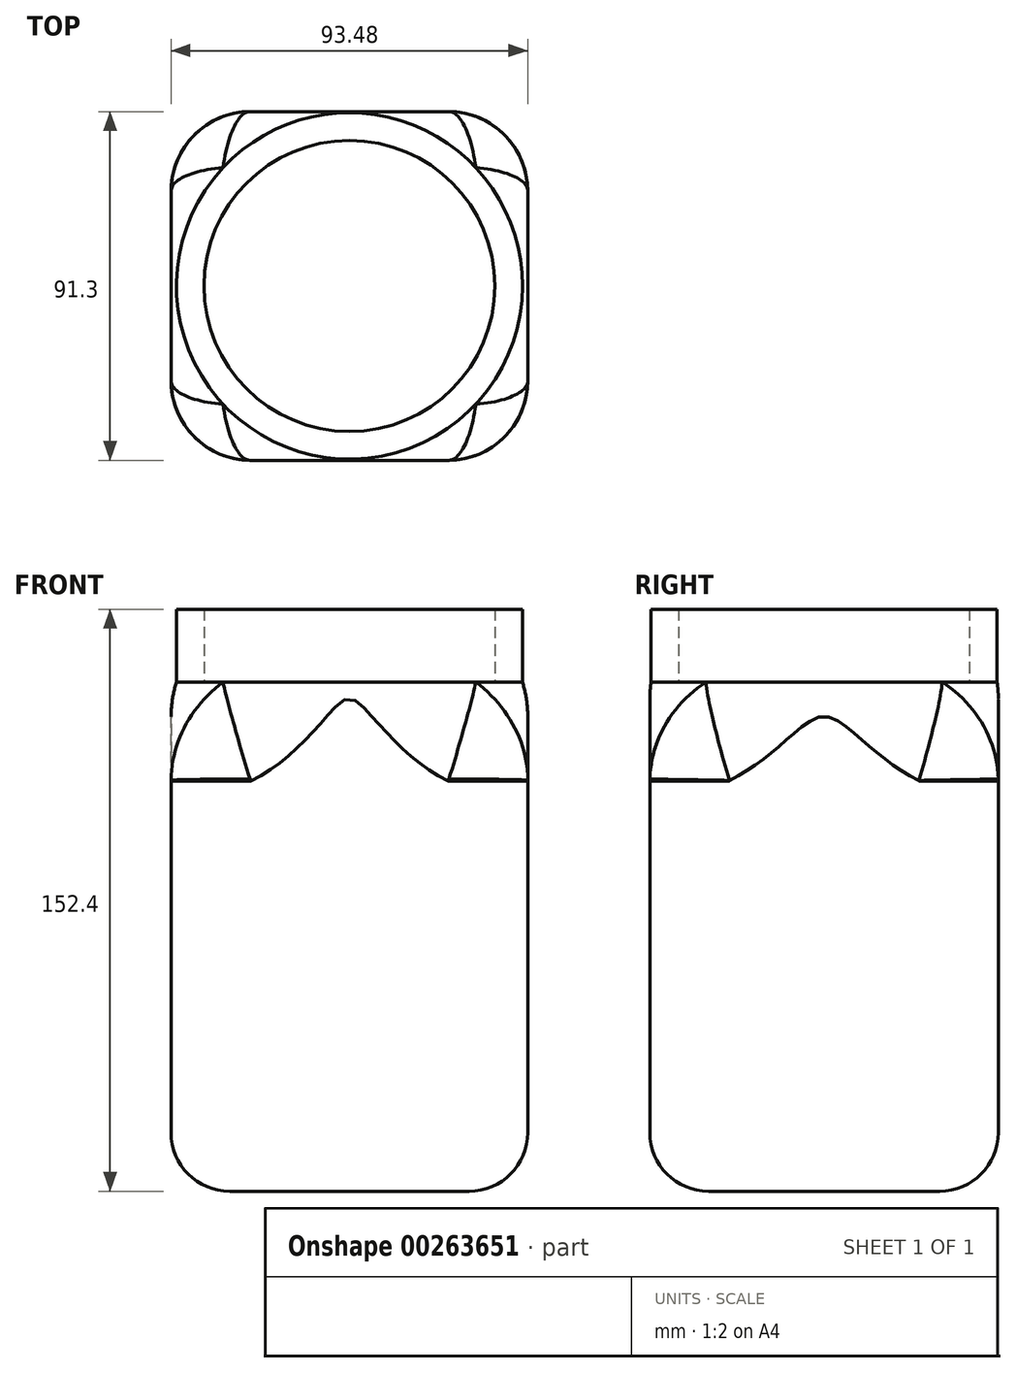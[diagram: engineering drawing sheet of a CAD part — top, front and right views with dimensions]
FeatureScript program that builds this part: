
annotation { "Feature Type Name" : "Feature", "Feature Type Description" : "" }
export const myFeature = defineFeature(function(context is Context, id is Id, definition is map)
    precondition{}
    {
        {
            var Q0;
            Q0=qCreatedBy(makeId("Top.planeOp"),FACE);
            var sketch = newSketch(context, id + "F0", { "sketchPlane" : qUnion([Q0])});
            skCircle(sketch, "E0", {"center": v(0, 0) * mm, "radius": 45.34 * mm});
            skSolve(sketch);
        }
        {
            var Q0;
            Q0 = qSketchRegion(id + "F0", true);
            extrude(context, id + "F1", {"entities" : qUnion([Q0]), "depth" : 19.05 * mm});
        }
        {
            var Q0;
            Q0=qCreatedBy(makeId("Top.planeOp"),FACE);
            var sketch = newSketch(context, id + "F2", { "sketchPlane" : qUnion([Q0])});
            skLineSegment(sketch, "E1.bottom", {"start": v(46.74, -45.65) * mm, "end": v(-46.74, -45.65) * mm});
            skLineSegment(sketch, "E1.top", {"start": v(46.74, 45.65) * mm, "end": v(-46.74, 45.65) * mm});
            skLineSegment(sketch, "E1.left", {"start": v(46.74, -45.65) * mm, "end": v(46.74, 45.65) * mm});
            skLineSegment(sketch, "E1.right", {"start": v(-46.74, -45.65) * mm, "end": v(-46.74, 45.65) * mm});
            skPoint(sketch, "E1.middle", {"position": v(0, 0) * mm});
            skSolve(sketch);
        }
        {
            var Q0;
            Q0=makeQuery(id+"F2.imprint","IMPRINT",FACE,{"disambiguationData":[TD([[makeQuery(id+"F2.imprint","IMPRINT",EDGE,{"derivedFrom":sQuery(id+"F2.wireOp",EDGE,"E1.bottom")}),-1.0]])]});
            extrude(context, id + "F3", {"entities" : qUnion([Q0]), "operationType" : NewBodyOperationType.ADD, "oppositeDirection" : true, "depth" : 133.35 * mm});
        }
        {
            var Q0;
            Q0=makeQuery(id+"F3.opExtrude","SWEPT_EDGE",EDGE,{"disambiguationData":[OSD([sQuery(id+"F2.wireOp",EDGE,"E1.bottom"),sQuery(id+"F2.wireOp",EDGE,"E1.right")])]});
            var Q1;
            Q1=makeQuery(id+"F3.opExtrude","SWEPT_EDGE",EDGE,{"disambiguationData":[OSD([sQuery(id+"F2.wireOp",EDGE,"E1.top"),sQuery(id+"F2.wireOp",EDGE,"E1.right")])]});
            fillet(context, id + "F4", {"entities" : qUnion([Q0, Q1]), "radius" : 20.85 * mm, "tangentPropagation" : true, "allowEdgeOverflow" : false});
        }
        {
            var Q0;
            Q0=makeQuery(id+"F3.opExtrude","SWEPT_EDGE",EDGE,{"disambiguationData":[OSD([sQuery(id+"F2.wireOp",EDGE,"E1.bottom"),sQuery(id+"F2.wireOp",EDGE,"E1.left")])]});
            var Q1;
            Q1=makeQuery(id+"F3.opExtrude","SWEPT_EDGE",EDGE,{"disambiguationData":[OSD([sQuery(id+"F2.wireOp",EDGE,"E1.top"),sQuery(id+"F2.wireOp",EDGE,"E1.left")])]});
            fillet(context, id + "F5", {"entities" : qUnion([Q0, Q1]), "radius" : 20.85 * mm, "tangentPropagation" : true, "allowEdgeOverflow" : false});
        }
        {
            var Q0;
            Q0=makeQuery(id+"F3.opExtrude","CAP_EDGE",EDGE,{"disambiguationData":[OSD([sQuery(id+"F2.wireOp",EDGE,"E1.left")])],"isStart":false});
            var Q1;
            {var subQ0=sQuery(id+"F2.wireOp",EDGE,"E1.left");var subQ1=sQuery(id+"F2.wireOp",EDGE,"E1.top");Q1=makeQuery(id+"F5.opFillet","BLEND_EDGE",EDGE,{"blendedFrom":[makeQuery(id+"F3.opExtrude","SWEPT_EDGE",EDGE,{"disambiguationData":[OSD([subQ1,subQ0])]}),makeQuery(id+"F3.opExtrude","CAP_FACE",FACE,{"disambiguationData":[OSD([sQuery(id+"F2.wireOp",EDGE,"E1.bottom"),subQ1,subQ0,sQuery(id+"F2.wireOp",EDGE,"E1.right")])],"isStart":false})],"blendedInto":[makeQuery(id+"F3.opExtrude","CAP_FACE",FACE,{"disambiguationData":[OSD([sQuery(id+"F2.wireOp",EDGE,"E1.bottom"),subQ1,subQ0,sQuery(id+"F2.wireOp",EDGE,"E1.right")])],"isStart":false})]});}
            var Q2;
            Q2=makeQuery(id+"F3.opExtrude","CAP_EDGE",EDGE,{"disambiguationData":[OSD([sQuery(id+"F2.wireOp",EDGE,"E1.top")])],"isStart":false});
            var Q3;
            {var subQ0=sQuery(id+"F2.wireOp",EDGE,"E1.right");var subQ1=sQuery(id+"F2.wireOp",EDGE,"E1.top");Q3=makeQuery(id+"F4.opFillet","BLEND_EDGE",EDGE,{"blendedFrom":[makeQuery(id+"F3.opExtrude","SWEPT_EDGE",EDGE,{"disambiguationData":[OSD([subQ1,subQ0])]}),makeQuery(id+"F3.opExtrude","CAP_FACE",FACE,{"disambiguationData":[OSD([sQuery(id+"F2.wireOp",EDGE,"E1.bottom"),subQ1,sQuery(id+"F2.wireOp",EDGE,"E1.left"),subQ0])],"isStart":false})],"blendedInto":[makeQuery(id+"F3.opExtrude","CAP_FACE",FACE,{"disambiguationData":[OSD([sQuery(id+"F2.wireOp",EDGE,"E1.bottom"),subQ1,sQuery(id+"F2.wireOp",EDGE,"E1.left"),subQ0])],"isStart":false})]});}
            var Q4;
            Q4=makeQuery(id+"F3.opExtrude","CAP_EDGE",EDGE,{"disambiguationData":[OSD([sQuery(id+"F2.wireOp",EDGE,"E1.right")])],"isStart":false});
            var Q5;
            {var subQ0=sQuery(id+"F2.wireOp",EDGE,"E1.right");var subQ1=sQuery(id+"F2.wireOp",EDGE,"E1.bottom");Q5=makeQuery(id+"F4.opFillet","BLEND_EDGE",EDGE,{"blendedFrom":[makeQuery(id+"F3.opExtrude","SWEPT_EDGE",EDGE,{"disambiguationData":[OSD([subQ1,subQ0])]}),makeQuery(id+"F3.opExtrude","CAP_FACE",FACE,{"disambiguationData":[OSD([subQ1,sQuery(id+"F2.wireOp",EDGE,"E1.top"),sQuery(id+"F2.wireOp",EDGE,"E1.left"),subQ0])],"isStart":false})],"blendedInto":[makeQuery(id+"F3.opExtrude","CAP_FACE",FACE,{"disambiguationData":[OSD([subQ1,sQuery(id+"F2.wireOp",EDGE,"E1.top"),sQuery(id+"F2.wireOp",EDGE,"E1.left"),subQ0])],"isStart":false})]});}
            var Q6;
            Q6=makeQuery(id+"F3.opExtrude","CAP_EDGE",EDGE,{"disambiguationData":[OSD([sQuery(id+"F2.wireOp",EDGE,"E1.bottom")])],"isStart":false});
            var Q7;
            {var subQ0=sQuery(id+"F2.wireOp",EDGE,"E1.left");var subQ1=sQuery(id+"F2.wireOp",EDGE,"E1.bottom");Q7=makeQuery(id+"F5.opFillet","BLEND_EDGE",EDGE,{"blendedFrom":[makeQuery(id+"F3.opExtrude","SWEPT_EDGE",EDGE,{"disambiguationData":[OSD([subQ1,subQ0])]}),makeQuery(id+"F3.opExtrude","CAP_FACE",FACE,{"disambiguationData":[OSD([subQ1,sQuery(id+"F2.wireOp",EDGE,"E1.top"),subQ0,sQuery(id+"F2.wireOp",EDGE,"E1.right")])],"isStart":false})],"blendedInto":[makeQuery(id+"F3.opExtrude","CAP_FACE",FACE,{"disambiguationData":[OSD([subQ1,sQuery(id+"F2.wireOp",EDGE,"E1.top"),subQ0,sQuery(id+"F2.wireOp",EDGE,"E1.right")])],"isStart":false})]});}
            fillet(context, id + "F6", {"entities" : qUnion([Q0, Q1, Q2, Q3, Q4, Q5, Q6, Q7]), "radius" : 15.33 * mm, "tangentPropagation" : true, "allowEdgeOverflow" : false});
        }
        {
            var Q0;
            Q0=makeQuery(id+"F3.opExtrude","CAP_EDGE",EDGE,{"disambiguationData":[OSD([sQuery(id+"F2.wireOp",EDGE,"E1.bottom")])],"isStart":true});
            fillet(context, id + "F7", {"entities" : qUnion([Q0]), "radius" : 30.05 * mm, "tangentPropagation" : true, "allowEdgeOverflow" : false});
        }
        {
            var Q0;
            Q0=qCreatedBy(makeId("Top.planeOp"),FACE);
            var sketch = newSketch(context, id + "F8", { "sketchPlane" : qUnion([Q0])});
            skCircle(sketch, "E2", {"center": v(0, 0) * mm, "radius": 31.45 * mm});
            skSolve(sketch);
        }
        {
            var Q0;
            Q0=sQuery(id+"F8.wireOp",VERTEX,"E2.center");
            var Q1;
            Q1=makeQuery(id+"F1.opExtrude","SWEPT_BODY",BODY,{"disambiguationData":[OSD([sQuery(id+"F0.wireOp",EDGE,"E0")])]});
            hole(context, id + "F9", {"style" : HoleStyle.SIMPLE, "endStyle" : HoleEndStyle.BLIND, "oppositeDirection" : true, "holeDiameter" : 76.2 * mm, "holeDepth" : 152.4 * mm, "tappedDepth" : 12.7 * mm, "tapClearance" : 3, "locations" : qUnion([Q0]), "scope" : qUnion([Q1])});
        }
    });
